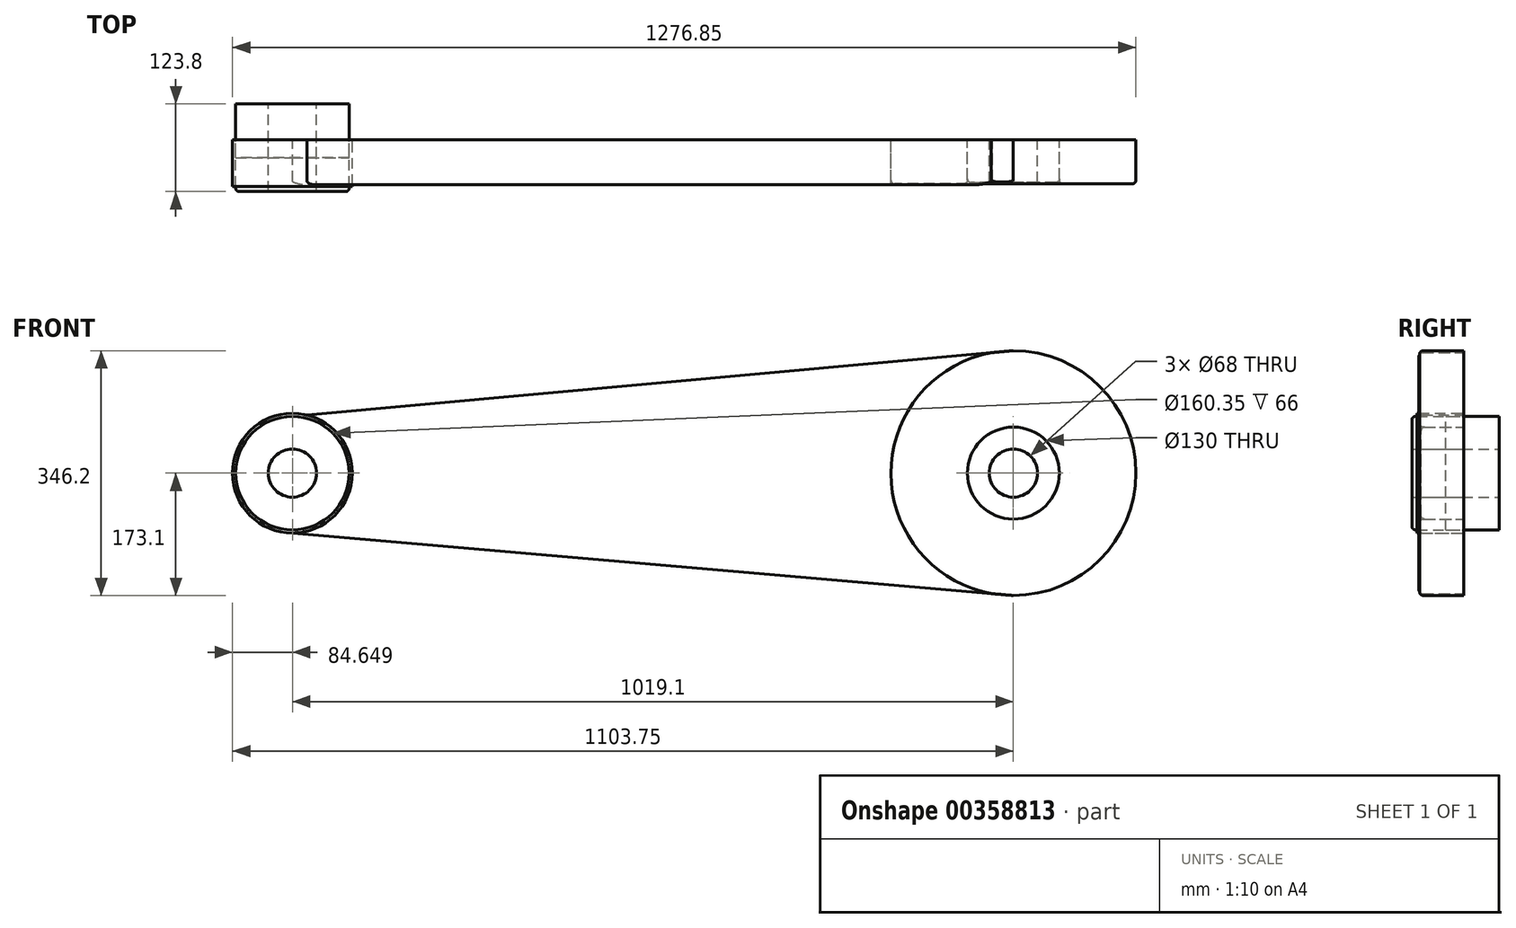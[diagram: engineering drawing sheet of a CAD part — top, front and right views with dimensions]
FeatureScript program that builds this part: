
annotation { "Feature Type Name" : "Feature", "Feature Type Description" : "" }
export const myFeature = defineFeature(function(context is Context, id is Id, definition is map)
    precondition{}
    {
        {
            var Q0;
            Q0=qCreatedBy(makeId("Front.planeOp"),FACE);
            var sketch = newSketch(context, id + "F0", { "sketchPlane" : qUnion([Q0])});
            skCircle(sketch, "E0", {"center": v(835.35, 0) * mm, "radius": 34 * mm});
            skCircle(sketch, "E1", {"center": v(835.35, 0) * mm, "radius": 65 * mm});
            skCircle(sketch, "E2", {"center": v(-183.75, 0) * mm, "radius": 34 * mm});
            skCircle(sketch, "E3", {"center": v(-183.75, 0) * mm, "radius": 80.17 * mm});
            skLineSegment(sketch, "E4", {"start": v(-183.75, 0) * mm, "end": v(835.35, 0) * mm, "construction": true});
            skCircle(sketch, "E5", {"center": v(-183.75, 0) * mm, "radius": 84.65 * mm});
            skCircle(sketch, "E6", {"center": v(835.35, 0) * mm, "radius": 173.1 * mm});
            skLineSegment(sketch, "E7", {"start": v(-183.75, 80.17) * mm, "end": v(835.35, 173.1) * mm});
            skLineSegment(sketch, "E8", {"start": v(-183.75, -84.65) * mm, "end": v(835.35, -173.1) * mm});
            skSolve(sketch);
        }
        {
            var Q0;
            Q0=makeQuery(id+"F0.imprint","IMPRINT",FACE,{"disambiguationData":[TD([[makeQuery(id+"F0.imprint","IMPRINT",EDGE,{"derivedFrom":sQuery(id+"F0.wireOp",EDGE,"E0")}),-1.0]])]});
            extrude(context, id + "F1", {"entities" : qUnion([Q0]), "depth" : 60 * mm, "offsetDistance" : 25 * mm});
        }
        {
            var Q0;
            Q0=makeQuery(id+"F0.imprint","IMPRINT",FACE,{"disambiguationData":[TD([[makeQuery(id+"F0.imprint","IMPRINT",EDGE,{"derivedFrom":sQuery(id+"F0.wireOp",EDGE,"E2")}),-1.0]])]});
            extrude(context, id + "F2", {"entities" : qUnion([Q0]), "depth" : 73 * mm, "offsetDistance" : 25 * mm});
        }
        {
            var Q0;
            Q0=makeQuery(id+"F2.opExtrude","CAP_EDGE",EDGE,{"disambiguationData":[OSD([sQuery(id+"F0.wireOp",EDGE,"E3")])],"isStart":false});
            fillet(context, id + "F3", {"entities" : qUnion([Q0]), "radius" : 5 * mm, "tangentPropagation" : true, "allowEdgeOverflow" : false});
        }
        {
            var Q0;
            Q0=makeQuery(id+"F1.opExtrude","CAP_EDGE",EDGE,{"disambiguationData":[OSD([sQuery(id+"F0.wireOp",EDGE,"E1")])],"isStart":false});
            var Q1;
            Q1=makeQuery(id+"FW1UkQRvboYkDOB_0.opExtrude","CAP_EDGE",EDGE,{"disambiguationData":[OSD([sQuery(id+"F0.wireOp",EDGE,"fBJ30h5k-k5Us-Y9C0-Q6bH-GX9qte7BnNYA")])],"isStart":false});
            var Q2;
            Q2=makeQuery(id+"FW1UkQRvboYkDOB_0.opExtrude","CAP_EDGE",EDGE,{"disambiguationData":[OSD([sQuery(id+"F0.wireOp",EDGE,"0Kp1RnWl-3cOE-GBpf-7H51-xnLNjGT4aQ9O")])],"isStart":false});
            fillet(context, id + "F4", {"entities" : qUnion([Q0, Q1, Q2]), "radius" : 5 * mm, "tangentPropagation" : true, "allowEdgeOverflow" : false});
        }
        {
            var Q0;
            Q0=qCreatedBy(makeId("Front.planeOp"),FACE);
            var sketch = newSketch(context, id + "F5", { "sketchPlane" : qUnion([Q0])});
            skCircle(sketch, "E9", {"center": v(834.97, 0) * mm, "radius": 37.82 * mm});
            skSolve(sketch);
        }
        {
            var Q0;
            Q0=sQuery(id+"F5.wireOp",EDGE,"E9");
            extrude(context, id + "F6", {"bodyType" : ToolBodyType.SURFACE, "surfaceEntities" : qUnion([Q0]), "oppositeDirection" : true, "depth" : 150 * mm});
        }
        {
            var Q0;
            Q0=makeQuery(id+"F0.imprint","IMPRINT",FACE,{"disambiguationData":[TD([[makeQuery(id+"F0.imprint","IMPRINT",EDGE,{"derivedFrom":sQuery(id+"F0.wireOp",EDGE,"E1")}),-1.0]])]});
            extrude(context, id + "F7", {"entities" : qUnion([Q0]), "depth" : 62 * mm, "offsetDistance" : 25 * mm});
        }
        {
            var Q0;
            Q0=makeQuery(id+"F2.opExtrude","CAP_FACE",FACE,{"disambiguationData":[OSD([sQuery(id+"F0.wireOp",EDGE,"E2"),sQuery(id+"F0.wireOp",EDGE,"E3")])],"isStart":true});
            extrude(context, id + "F8", {"entities" : qUnion([Q0]), "oppositeDirection" : true, "depth" : 25 * mm, "offsetDistance" : 25 * mm, "hasSecondDirection" : true, "secondDirectionOppositeDirection" : false, "secondDirectionDepth" : 50.8 * mm});
        }
        {
            var Q0;
            Q0=makeQuery(id+"F0.imprint","IMPRINT",FACE,{"disambiguationData":[TD([[makeQuery(id+"F0.imprint","IMPRINT",EDGE,{"derivedFrom":sQuery(id+"F0.wireOp",EDGE,"E3")}),-1.0]])]});
            var Q1;
            {var subQ0=sQuery(id+"F0.wireOp",EDGE,"MlWKoV2a-Rgpy-fjN7-13CX-QezHCS82g9wR");var subQ1=sQuery(id+"F0.wireOp",EDGE,"Yd3i7Te2-7NrN-uItW-KDtD-10ETbKpohEa0");var subQ2=makeQuery(id+"F0.imprint","INTERSECT",VERTEX,{"disambiguationData":[OD(0.0)],"derivedFrom":[subQ1,subQ0]});Q1=makeQuery(id+"F0.imprint","IMPRINT",FACE,{"disambiguationData":[TD([[makeQuery(id+"F0.imprint","IMPRINT",EDGE,{"disambiguationData":[TD([[subQ2,-1.0]])],"derivedFrom":subQ1}),1.0]])]});}
            extrude(context, id + "F9", {"entities" : qUnion([Q0, Q1]), "depth" : 66 * mm, "offsetDistance" : 25 * mm});
        }
        {
            var Q0;
            {var subQ0=sQuery(id+"F0.wireOp",EDGE,"6ffpRjFu-mErr-uLBe-kyIE-VOIxPUzilDHI");var subQ1=sQuery(id+"F0.wireOp",EDGE,"E5");var subQ2=makeQuery(id+"F0.imprint","INTERSECT",VERTEX,{"derivedFrom":[subQ1,subQ0]});Q0=makeQuery(id+"F0.imprint","IMPRINT",FACE,{"disambiguationData":[TD([[makeQuery(id+"F0.imprint","IMPRINT",EDGE,{"disambiguationData":[TD([[subQ2,1.0]])],"derivedFrom":subQ1}),-1.0]])]});}
            extrude(context, id + "F10", {"entities" : qUnion([Q0]), "depth" : 63.5 * mm, "offsetDistance" : 25 * mm});
        }
        {
            var Q0;
            {var subQ0=sQuery(id+"F0.wireOp",EDGE,"E6");Q0=makeQuery(id+"F7.opExtrude","CAP_EDGE",EDGE,{"disambiguationData":[OSD([subQ0]),TDD([makeQuery(id+"F0.imprint","IMPRINT",EDGE,{"disambiguationData":[TD([[makeQuery(id+"F0.imprint","INTERSECT",VERTEX,{"disambiguationData":[OD(1.0)],"derivedFrom":[subQ0,sQuery(id+"F0.wireOp",EDGE,"E7")]}),-1.0]])],"derivedFrom":subQ0})])],"isStart":false});}
            fillet(context, id + "F11", {"entities" : qUnion([Q0]), "radius" : 5 * mm, "tangentPropagation" : true, "allowEdgeOverflow" : false});
        }
        {
            var Q0;
            Q0=makeQuery(id+"F7.opExtrude","CAP_EDGE",EDGE,{"disambiguationData":[OSD([sQuery(id+"F0.wireOp",EDGE,"E1")])],"isStart":false});
            fillet(context, id + "F12", {"entities" : qUnion([Q0]), "radius" : 5 * mm, "tangentPropagation" : true, "allowEdgeOverflow" : false});
        }
        {
            var Q0;
            Q0=makeQuery(id+"F10.opExtrude","CAP_EDGE",EDGE,{"disambiguationData":[OSD([sQuery(id+"F0.wireOp",EDGE,"E7")])],"isStart":false});
            var Q1;
            Q1=makeQuery(id+"F10.opExtrude","CAP_EDGE",EDGE,{"disambiguationData":[OSD([sQuery(id+"F0.wireOp",EDGE,"E8")])],"isStart":false});
            fillet(context, id + "F13", {"entities" : qUnion([Q0, Q1]), "radius" : 5 * mm, "tangentPropagation" : true, "allowEdgeOverflow" : false});
        }
    });
